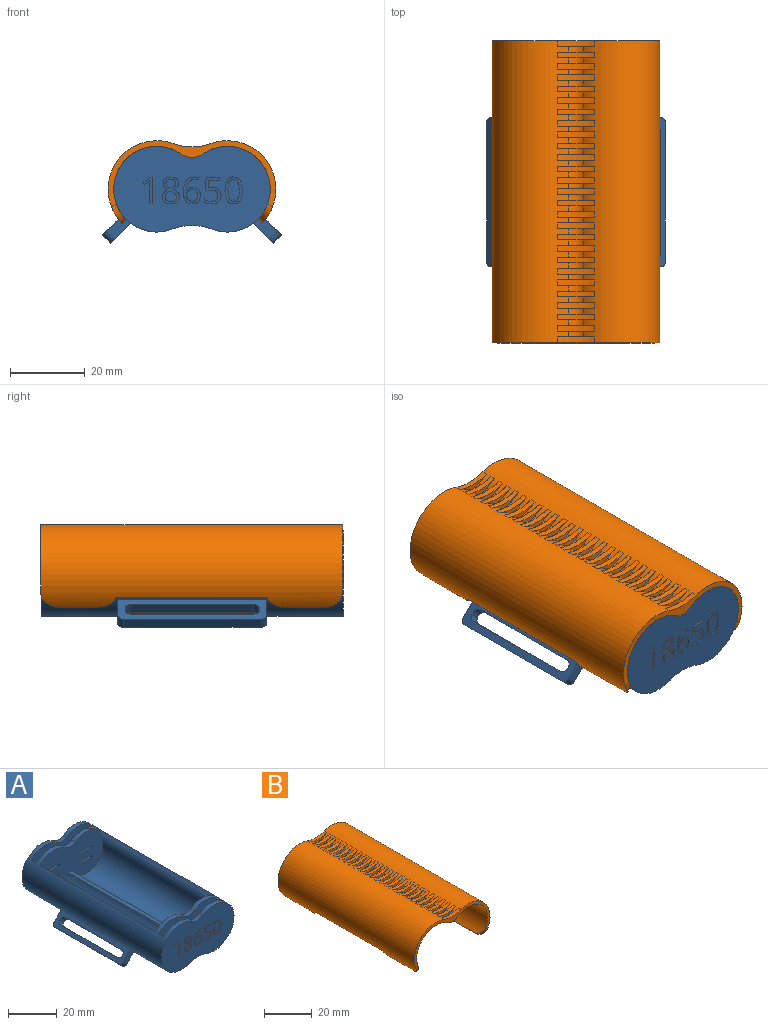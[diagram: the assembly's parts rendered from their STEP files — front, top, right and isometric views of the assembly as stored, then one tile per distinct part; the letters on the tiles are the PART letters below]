
ASSEMBLY  parts=2 mates=1
PART A: 205 faces, bbox 48x81x26 mm
  f0: plane 42x23mm, normal (0,-1,0), area 718.4mm2, adj f3,f9,f52,f88,f89,f90,f91,f92
  f1: plane 40x5.37mm, normal (0.71,0,-0.71), area 175.3mm2, adj f3,f23,f24,f39,f40,f41,f42,f43
  f2: plane 40x5.37mm, normal (-0.71,0,0.71), area 175.3mm2, adj f3,f23,f24,f39,f40,f41,f42,f43
  f3: cylinder r=11.5mm len=81mm, axis (0,1,0), area 2543.9mm2, adj f0,f1,f2,f4,f5,f8,f9,f20
  f4: plane 38x21mm, normal (0,1,0), area 630.6mm2, adj f3,f10,f11,f12,f13,f14,f15,f16
  f5: plane 38x21mm, normal (0,-1,0), area 630.6mm2, adj f3,f6,f7,f8,f10,f11,f12,f13
  f6: plane 67x1.77mm, normal (0,0,1), area 118.3mm2, adj f5,f7,f26,f53
  f7: cylinder r=9.5mm len=67mm, axis (0,1,0), area 2222.9mm2, adj f5,f6,f8,f26
  f8: plane 67x1.41mm, normal (0.71,0,0.71), area 134mm2, adj f3,f5,f7,f26
  f9: cylinder r=15mm len=81mm, axis (0,1,0), area 891mm2, adj f0,f3,f22,f52
  f10: plane 2x1mm, normal (-1,0,0), area 2mm2, adj f4,f5,f11,f13
  f11: plane 6x2mm, normal (0,0,1), area 12mm2, adj f4,f5,f10,f12
  f12: plane 2x1mm, normal (1,0,0), area 2mm2, adj f4,f5,f11,f13
  f13: plane 6x2mm, normal (0,0,-1), area 12mm2, adj f4,f5,f10,f12
  f14: plane 6x2mm, normal (0,0,1), area 12mm2, adj f4,f5,f15,f17
  f15: plane 2x1mm, normal (1,0,0), area 2mm2, adj f4,f5,f14,f16
  f16: plane 6x2mm, normal (0,0,-1), area 12mm2, adj f4,f5,f15,f17
  f17: plane 2x1mm, normal (-1,0,0), area 2mm2, adj f4,f5,f14,f16
  f18: plane 3x1.77mm, normal (0,0,1), area 5.3mm2, adj f4,f19,f21,f63
  f19: cylinder r=9.5mm len=18.12mm, axis (0,-1,0), area 99.5mm2, adj f4,f18,f20,f21
  f20: plane 3x1.41mm, normal (0.71,0,0.71), area 6mm2, adj f3,f4,f19,f21
  f21: plane 38x21mm, normal (0,-1,0), area 641.7mm2, adj f3,f18,f19,f20,f52,f63,f64,f197
  f22: plane 42x23mm, normal (0,1,0), area 797.6mm2, adj f3,f9,f52,f197,f198,f199,f200,f203
  f23: plane 37x2.14mm, normal (-0.71,0,-0.71), area 111.8mm2, adj f1,f2,f48,f49
  f24: plane 6.44x6.44mm, normal (0,1,0), area 18.2mm2, adj f1,f2,f3,f49
  f25: plane 38x21mm, normal (0,-1,0), area 630.6mm2, adj f3,f27,f28,f29,f30,f31,f32,f33
  f26: plane 38x21mm, normal (0,1,0), area 630.6mm2, adj f3,f6,f7,f8,f27,f28,f29,f30
  f27: plane 2x1mm, normal (-1,0,0), area 2mm2, adj f25,f26,f28,f30
  f28: plane 6x2mm, normal (0,0,1), area 12mm2, adj f25,f26,f27,f29
  f29: plane 2x1mm, normal (1,0,0), area 2mm2, adj f25,f26,f28,f30
  f30: plane 6x2mm, normal (0,0,-1), area 12mm2, adj f25,f26,f27,f29
  f31: plane 6x2mm, normal (0,0,1), area 12mm2, adj f25,f26,f32,f34
  f32: plane 2x1mm, normal (1,0,0), area 2mm2, adj f25,f26,f31,f33
  f33: plane 6x2mm, normal (0,0,-1), area 12mm2, adj f25,f26,f32,f34
  f34: plane 2x1mm, normal (-1,0,0), area 2mm2, adj f25,f26,f31,f33
  f35: plane 3x1.77mm, normal (0,0,1), area 5.3mm2, adj f25,f36,f38,f75
  f36: cylinder r=9.5mm len=18.12mm, axis (0,1,0), area 99.5mm2, adj f25,f35,f37,f38
  f37: plane 3x1.41mm, normal (0.71,0,0.71), area 6mm2, adj f3,f25,f36,f38
  f38: plane 38x21mm, normal (0,1,0), area 654.6mm2, adj f3,f35,f36,f37,f52,f75,f76,f202
  f39: plane 6.44x6.44mm, normal (0,-1,0), area 18.2mm2, adj f1,f2,f3,f48
  f40: plane 2.55x2.55mm, normal (0,1,0), area 1.8mm2, adj f1,f2,f44,f47
  f41: plane 33x2.14mm, normal (-0.71,0,-0.71), area 99.7mm2, adj f1,f2,f44,f45
  f42: plane 2.55x2.55mm, normal (0,-1,0), area 1.8mm2, adj f1,f2,f45,f46
  f43: plane 33x2.14mm, normal (0.71,0,0.71), area 99.7mm2, adj f1,f2,f46,f47
  f44: cylinder r=1.5mm len=3.2mm, axis (0.71,0,-0.71), area 7.1mm2, adj f1,f2,f40,f41
  f45: cylinder r=1.5mm len=3.2mm, axis (-0.71,0,0.71), area 7.1mm2, adj f1,f2,f41,f42
  f46: cylinder r=1.5mm len=3.2mm, axis (0.71,0,-0.71), area 7.1mm2, adj f1,f2,f42,f43
  f47: cylinder r=1.5mm len=3.2mm, axis (-0.71,0,0.71), area 7.1mm2, adj f1,f2,f40,f43
  f48: cylinder r=1.5mm len=3.2mm, axis (-0.71,0,0.71), area 7.1mm2, adj f1,f2,f23,f39
  f49: cylinder r=1.5mm len=3.2mm, axis (-0.71,0,0.71), area 7.1mm2, adj f1,f2,f23,f24
  f50: plane 40x5.37mm, normal (-0.71,0,-0.71), area 175.3mm2, adj f52,f65,f66,f77,f78,f79,f80,f81
  f51: plane 40x5.37mm, normal (0.71,0,0.71), area 175.3mm2, adj f52,f65,f66,f77,f78,f79,f80,f81
  f52: cylinder r=11.5mm len=81mm, axis (0,1,0), area 2543.9mm2, adj f0,f4,f5,f9,f21,f22,f25,f26
  f53: cylinder r=9.5mm len=67mm, axis (0,1,0), area 2222.9mm2, adj f5,f6,f26,f54
  f54: plane 67x1.41mm, normal (-0.71,0,0.71), area 134mm2, adj f5,f26,f52,f53
  f55: plane 2x1mm, normal (1,0,0), area 2mm2, adj f4,f5,f56,f58
  f56: plane 6x2mm, normal (0,0,1), area 12mm2, adj f4,f5,f55,f57
  f57: plane 2x1mm, normal (-1,0,0), area 2mm2, adj f4,f5,f56,f58
  f58: plane 6x2mm, normal (0,0,-1), area 12mm2, adj f4,f5,f55,f57
  f59: plane 6x2mm, normal (0,0,1), area 12mm2, adj f4,f5,f60,f62
  f60: plane 2x1mm, normal (-1,0,0), area 2mm2, adj f4,f5,f59,f61
  f61: plane 6x2mm, normal (0,0,-1), area 12mm2, adj f4,f5,f60,f62
  f62: plane 2x1mm, normal (1,0,0), area 2mm2, adj f4,f5,f59,f61
  f63: cylinder r=9.5mm len=18.12mm, axis (0,-1,0), area 99.5mm2, adj f4,f18,f21,f64
  f64: plane 3x1.41mm, normal (-0.71,0,0.71), area 6mm2, adj f4,f21,f52,f63
  f65: plane 37x2.14mm, normal (0.71,0,-0.71), area 111.8mm2, adj f50,f51,f86,f87
  f66: plane 6.44x6.44mm, normal (0,1,0), area 18.2mm2, adj f50,f51,f52,f87
  f67: plane 2x1mm, normal (1,0,0), area 2mm2, adj f25,f26,f68,f70
  f68: plane 6x2mm, normal (0,0,1), area 12mm2, adj f25,f26,f67,f69
  f69: plane 2x1mm, normal (-1,0,0), area 2mm2, adj f25,f26,f68,f70
  f70: plane 6x2mm, normal (0,0,-1), area 12mm2, adj f25,f26,f67,f69
  f71: plane 6x2mm, normal (0,0,1), area 12mm2, adj f25,f26,f72,f74
  f72: plane 2x1mm, normal (-1,0,0), area 2mm2, adj f25,f26,f71,f73
  f73: plane 6x2mm, normal (0,0,-1), area 12mm2, adj f25,f26,f72,f74
  f74: plane 2x1mm, normal (1,0,0), area 2mm2, adj f25,f26,f71,f73
  f75: cylinder r=9.5mm len=18.12mm, axis (0,1,0), area 99.5mm2, adj f25,f35,f38,f76
  f76: plane 3x1.41mm, normal (-0.71,0,0.71), area 6mm2, adj f25,f38,f52,f75
  f77: plane 6.44x6.44mm, normal (0,-1,0), area 18.2mm2, adj f50,f51,f52,f86
  f78: plane 2.55x2.55mm, normal (0,1,0), area 1.8mm2, adj f50,f51,f82,f85
  f79: plane 33x2.14mm, normal (0.71,0,-0.71), area 99.7mm2, adj f50,f51,f82,f83
  f80: plane 2.55x2.55mm, normal (0,-1,0), area 1.8mm2, adj f50,f51,f83,f84
  f81: plane 33x2.14mm, normal (-0.71,0,0.71), area 99.7mm2, adj f50,f51,f84,f85
  f82: cylinder r=1.5mm len=3.2mm, axis (-0.71,0,-0.71), area 7.1mm2, adj f50,f51,f78,f79
  f83: cylinder r=1.5mm len=3.2mm, axis (0.71,0,0.71), area 7.1mm2, adj f50,f51,f79,f80
  f84: cylinder r=1.5mm len=3.2mm, axis (-0.71,0,-0.71), area 7.1mm2, adj f50,f51,f80,f81
  f85: cylinder r=1.5mm len=3.2mm, axis (0.71,0,0.71), area 7.1mm2, adj f50,f51,f78,f81
  f86: cylinder r=1.5mm len=3.2mm, axis (0.71,0,0.71), area 7.1mm2, adj f50,f51,f65,f77
  f87: cylinder r=1.5mm len=3.2mm, axis (0.71,0,0.71), area 7.1mm2, adj f50,f51,f65,f66
  f88: extruded ~1.1x0.5mm, area 0.6mm2, adj f0,f89,f106,f107
  f89: plane 2.11x0.5mm, normal (-1,0,0.08), area 1.1mm2, adj f0,f88,f90,f107
  f90: plane 2.81x0.5mm, normal (0,0,1), area 1.4mm2, adj f0,f89,f91,f107
  f91: plane 0.73x0.5mm, normal (-1,0,0), area 0.4mm2, adj f0,f90,f92,f107
  f92: plane 3.49x0.5mm, normal (0,0,-1), area 1.7mm2, adj f0,f91,f93,f107
  f93: plane 3.28x0.5mm, normal (1,0,-0.08), area 1.6mm2, adj f0,f92,f94,f107
  f94: plane 0.5x0.41mm, normal (0.54,0,0.84), area 0.2mm2, adj f0,f93,f95,f107
  f95: extruded ~1.22x0.5mm, area 0.6mm2, adj f0,f94,f96,f107
  f96: extruded ~1.8x1.47mm, area 1.3mm2, adj f0,f95,f97,f107
  f97: extruded ~1.15x0.5mm, area 0.6mm2, adj f0,f96,f98,f107
  f98: extruded ~1.31x0.5mm, area 0.7mm2, adj f0,f97,f99,f107
  f99: extruded ~0.98x0.5mm, area 0.5mm2, adj f0,f98,f100,f107
  f100: extruded ~0.83x0.5mm, area 0.5mm2, adj f0,f99,f101,f107
  f101: plane 0.77x0.5mm, normal (1,0,0), area 0.4mm2, adj f0,f100,f102,f107
  f102: extruded ~1.81x0.5mm, area 0.9mm2, adj f0,f101,f103,f107
  f103: extruded ~1.91x0.62mm, area 1mm2, adj f0,f102,f104,f107
  f104: extruded ~1.71x0.69mm, area 1mm2, adj f0,f103,f105,f107
  f105: extruded ~1.5x0.64mm, area 0.8mm2, adj f0,f104,f106,f107
  f106: extruded ~1.74x0.55mm, area 0.9mm2, adj f0,f88,f105,f107
  f107: plane 7.11x4.41mm, normal (0,-1,0), area 11.4mm2, adj f88,f89,f90,f91,f92,f93,f94,f95
  f108: extruded ~2.28x0.64mm, area 1.2mm2, adj f0,f109,f132,f133
  f109: extruded ~1.73x0.82mm, area 1mm2, adj f0,f108,f110,f133
  f110: extruded ~1.61x0.63mm, area 0.9mm2, adj f0,f109,f111,f133
  f111: extruded ~1.72x0.6mm, area 0.9mm2, adj f0,f110,f112,f133
  f112: extruded ~1.55x0.54mm, area 0.8mm2, adj f0,f111,f113,f133
  f113: extruded ~1.49x0.57mm, area 0.8mm2, adj f0,f112,f114,f133
  f114: extruded ~1.67x0.83mm, area 1mm2, adj f0,f113,f115,f133
  f115: plane 0.5x0.06mm, normal (0,0,-1), area 0mm2, adj f0,f114,f116,f133
  f116: extruded ~2.21x0.65mm, area 1.2mm2, adj f0,f115,f117,f133
  f117: extruded ~1.72x0.7mm, area 1mm2, adj f0,f116,f118,f133
  f118: extruded ~0.84x0.5mm, area 0.4mm2, adj f0,f117,f119,f133
  f119: plane 0.69x0.5mm, normal (-1,0,0), area 0.3mm2, adj f0,f118,f120,f133
  f120: extruded ~0.85x0.5mm, area 0.4mm2, adj f0,f119,f121,f133
  f121: extruded ~2.38x1.02mm, area 1.3mm2, adj f0,f120,f132,f133
  f122: extruded ~0.8x0.5mm, area 0.4mm2, adj f123,f131,f133,f134
  f123: extruded ~0.68x0.54mm, area 0.4mm2, adj f122,f124,f133,f134
  f124: extruded ~0.92x0.5mm, area 0.5mm2, adj f123,f125,f133,f134
  f125: extruded ~0.65x0.5mm, area 0.3mm2, adj f124,f126,f133,f134
  f126: extruded ~0.57x0.5mm, area 0.4mm2, adj f125,f127,f133,f134
  f127: extruded ~0.79x0.5mm, area 0.4mm2, adj f126,f128,f133,f134
  f128: extruded ~1.05x0.5mm, area 0.6mm2, adj f127,f129,f133,f134
  f129: extruded ~1.09x0.5mm, area 0.6mm2, adj f128,f130,f133,f134
  f130: extruded ~1.24x0.5mm, area 0.7mm2, adj f129,f131,f133,f134
  f131: extruded ~1.06x0.5mm, area 0.6mm2, adj f122,f130,f133,f134
  f132: extruded ~3.09x0.8mm, area 1.6mm2, adj f0,f108,f121,f133
  f133: plane 7.21x4.58mm, normal (0,-1,0), area 12.7mm2, adj f108,f109,f110,f111,f112,f113,f114,f115
  f134: plane 3.16x2.97mm, normal (0,-1,0), area 7.6mm2, adj f122,f123,f124,f125,f126,f127,f128,f129
  f135: extruded ~2.68x0.59mm, area 1.4mm2, adj f0,f136,f150,f151
  f136: extruded ~1.73x0.93mm, area 1mm2, adj f0,f135,f137,f151
  f137: extruded ~1.74x0.89mm, area 1mm2, adj f0,f136,f138,f151
  f138: extruded ~2.72x0.57mm, area 1.4mm2, adj f0,f137,f139,f151
  f139: extruded ~2.69x0.59mm, area 1.4mm2, adj f0,f138,f140,f151
  f140: extruded ~1.72x0.92mm, area 1mm2, adj f0,f139,f141,f151
  f141: extruded ~1.75x0.9mm, area 1mm2, adj f0,f140,f150,f151
  f142: extruded ~2.22x0.5mm, area 1.1mm2, adj f143,f149,f151,f152
  f143: extruded ~1.15x0.69mm, area 0.7mm2, adj f142,f144,f151,f152
  f144: extruded ~1.15x0.7mm, area 0.7mm2, adj f143,f145,f151,f152
  f145: extruded ~2.21x0.5mm, area 1.1mm2, adj f144,f146,f151,f152
  f146: extruded ~2.22x0.5mm, area 1.1mm2, adj f145,f147,f151,f152
  f147: extruded ~1.15x0.71mm, area 0.7mm2, adj f146,f148,f151,f152
  f148: extruded ~1.15x0.7mm, area 0.7mm2, adj f147,f149,f151,f152
  f149: extruded ~2.23x0.5mm, area 1.1mm2, adj f142,f148,f151,f152
  f150: extruded ~2.72x0.57mm, area 1.4mm2, adj f0,f135,f141,f151
  f151: plane 7.22x4.64mm, normal (0,-1,0), area 13mm2, adj f135,f136,f137,f138,f139,f140,f141,f142
  f152: plane 5.84x3.02mm, normal (0,-1,0), area 14.9mm2, adj f142,f143,f144,f145,f146,f147,f148,f149
  f153: extruded ~1.51x0.5mm, area 0.8mm2, adj f0,f154,f183,f184
  f154: extruded ~1.22x0.56mm, area 0.7mm2, adj f0,f153,f155,f184
  f155: extruded ~0.97x0.5mm, area 0.5mm2, adj f0,f154,f156,f184
  f156: extruded ~0.95x0.81mm, area 0.6mm2, adj f0,f155,f157,f184
  f157: extruded ~1.88x1.47mm, area 1.3mm2, adj f0,f156,f158,f184
  f158: extruded ~1.39x0.6mm, area 0.8mm2, adj f0,f157,f159,f184
  f159: extruded ~1.73x0.5mm, area 0.9mm2, adj f0,f158,f160,f184
  f160: extruded ~1.67x0.52mm, area 0.9mm2, adj f0,f159,f161,f184
  f161: extruded ~1.39x0.61mm, area 0.8mm2, adj f0,f160,f162,f184
  f162: extruded ~1.04x0.5mm, area 0.6mm2, adj f0,f161,f163,f184
  f163: extruded ~1.21x0.86mm, area 0.7mm2, adj f0,f162,f164,f184
  f164: extruded ~1.03x0.78mm, area 0.6mm2, adj f0,f163,f165,f184
  f165: extruded ~0.95x0.5mm, area 0.5mm2, adj f0,f164,f166,f184
  f166: extruded ~1.23x0.56mm, area 0.7mm2, adj f0,f165,f183,f184
  f167: extruded ~0.89x0.5mm, area 0.5mm2, adj f168,f181,f184,f186
  f168: extruded ~1.04x0.68mm, area 0.6mm2, adj f167,f169,f184,f186
  f169: extruded ~1.3x0.7mm, area 0.7mm2, adj f168,f170,f184,f186
  f170: extruded ~0.83x0.5mm, area 0.5mm2, adj f169,f171,f184,f186
  f171: extruded ~0.92x0.5mm, area 0.5mm2, adj f170,f172,f184,f186
  f172: extruded ~1.11x0.5mm, area 0.6mm2, adj f171,f173,f184,f186
  f173: extruded ~1.12x0.5mm, area 0.6mm2, adj f172,f181,f184,f186
  f174: extruded ~0.96x0.5mm, area 0.5mm2, adj f175,f182,f184,f185
  f175: extruded ~0.77x0.5mm, area 0.4mm2, adj f174,f176,f184,f185
  f176: extruded ~0.77x0.5mm, area 0.4mm2, adj f175,f177,f184,f185
  f177: extruded ~0.97x0.62mm, area 0.6mm2, adj f176,f178,f184,f185
  f178: extruded ~1.05x0.63mm, area 0.6mm2, adj f177,f179,f184,f185
  f179: extruded ~0.76x0.5mm, area 0.4mm2, adj f178,f180,f184,f185
  f180: extruded ~0.77x0.5mm, area 0.4mm2, adj f179,f182,f184,f185
  f181: extruded ~0.9x0.5mm, area 0.5mm2, adj f167,f173,f184,f186
  f182: extruded ~0.94x0.5mm, area 0.5mm2, adj f174,f180,f184,f185
  f183: extruded ~1.52x0.5mm, area 0.8mm2, adj f0,f153,f166,f184
  f184: plane 7.21x4.61mm, normal (0,-1,0), area 14.6mm2, adj f153,f154,f155,f156,f157,f158,f159,f160
  f185: plane 2.59x2.45mm, normal (0,-1,0), area 4.8mm2, adj f174,f175,f176,f177,f178,f179,f180,f182
  f186: plane 3.04x2.79mm, normal (0,-1,0), area 6.4mm2, adj f167,f168,f169,f170,f171,f172,f173,f181
  f187: plane 7.01x0.5mm, normal (-1,0,0), area 3.5mm2, adj f0,f188,f195,f196
  f188: plane 0.67x0.5mm, normal (0,0,-1), area 0.3mm2, adj f0,f187,f189,f196
  f189: plane 1.86x1.44mm, normal (0.61,0,-0.79), area 1.2mm2, adj f0,f188,f190,f196
  f190: plane 0.55x0.5mm, normal (0.79,0,0.61), area 0.3mm2, adj f0,f189,f191,f196
  f191: extruded ~1.14x0.94mm, area 0.7mm2, adj f0,f190,f192,f196
  f192: extruded ~0.5x0.23mm, area 0.2mm2, adj f0,f191,f193,f196
  f193: extruded ~1.18x0.5mm, area 0.6mm2, adj f0,f192,f194,f196
  f194: plane 5x0.5mm, normal (1,0,0), area 2.5mm2, adj f0,f193,f195,f196
  f195: plane 0.78x0.5mm, normal (0,0,1), area 0.4mm2, adj f0,f187,f194,f196
  f196: plane 7.01x2.53mm, normal (0,-1,0), area 6.7mm2, adj f187,f188,f189,f190,f191,f192,f193,f194
  f197: cylinder r=1.5mm len=3mm, axis (0,1,0), area 10.4mm2, adj f21,f22,f199,f200
  f198: cylinder r=1.5mm len=3mm, axis (0,1,0), area 10.4mm2, adj f21,f22,f199,f200
  f199: cylinder r=5mm len=2mm, axis (0,1,0), area 3.1mm2, adj f21,f22,f197,f198
  f200: cylinder r=5mm len=2mm, axis (0,1,0), area 3.1mm2, adj f21,f22,f197,f198
  f201: cylinder r=5mm len=5.76mm, axis (0,-1,0), area 12.3mm2, adj f3,f25,f26,f52
  f202: cylinder r=5mm len=5.76mm, axis (0,-1,0), area 12.3mm2, adj f0,f3,f38,f52
  f203: cylinder r=5mm len=5.76mm, axis (0,1,0), area 12.3mm2, adj f3,f21,f22,f52
  f204: cylinder r=5mm len=5.76mm, axis (0,1,0), area 12.3mm2, adj f3,f4,f5,f52
PART B: 126 faces, bbox 45x81x23.1 mm
  f0: plane 10.6x1.06mm, normal (-0.71,0,-0.71), area 15.8mm2, adj f1,f34,f118,f121
  f1: cylinder r=13mm len=80.94mm, axis (0,1,0), area 2827.1mm2, adj f0,f2,f3,f4,f5,f6,f7,f8
  f2: cylinder r=3.5mm len=4.03mm, axis (0,1,0), area 6.7mm2, adj f1,f28,f113,f117
  f3: cylinder r=3.5mm len=4.03mm, axis (0,1,0), area 6.7mm2, adj f1,f28,f110,f114
  f4: cylinder r=3.5mm len=4.03mm, axis (0,1,0), area 6.7mm2, adj f1,f28,f107,f111
  f5: cylinder r=3.5mm len=4.03mm, axis (0,1,0), area 6.7mm2, adj f1,f28,f104,f108
  f6: cylinder r=3.5mm len=4.03mm, axis (0,1,0), area 6.7mm2, adj f1,f28,f101,f105
  f7: cylinder r=3.5mm len=4.03mm, axis (0,1,0), area 6.7mm2, adj f1,f28,f98,f102
  f8: cylinder r=3.5mm len=4.03mm, axis (0,1,0), area 6.7mm2, adj f1,f28,f95,f99
  f9: cylinder r=3.5mm len=4.03mm, axis (0,1,0), area 6.7mm2, adj f1,f28,f92,f96
  f10: cylinder r=3.5mm len=4.03mm, axis (0,1,0), area 6.7mm2, adj f1,f28,f89,f93
  f11: cylinder r=3.5mm len=4.03mm, axis (0,1,0), area 6.7mm2, adj f1,f28,f86,f90
  f12: cylinder r=3.5mm len=4.03mm, axis (0,1,0), area 6.7mm2, adj f1,f28,f83,f87
  f13: cylinder r=3.5mm len=4.03mm, axis (0,1,0), area 6.7mm2, adj f1,f28,f80,f84
  f14: cylinder r=3.5mm len=4.03mm, axis (0,1,0), area 6.7mm2, adj f1,f28,f77,f81
  f15: cylinder r=3.5mm len=4.03mm, axis (0,1,0), area 6.7mm2, adj f1,f28,f74,f78
  f16: cylinder r=3.5mm len=4.03mm, axis (0,1,0), area 6.7mm2, adj f1,f28,f71,f75
  f17: cylinder r=3.5mm len=4.03mm, axis (0,1,0), area 6.7mm2, adj f1,f28,f68,f72
  f18: cylinder r=3.5mm len=4.03mm, axis (0,1,0), area 6.7mm2, adj f1,f28,f65,f69
  f19: cylinder r=3.5mm len=4.03mm, axis (0,1,0), area 6.7mm2, adj f1,f28,f62,f66
  f20: cylinder r=3.5mm len=4.03mm, axis (0,1,0), area 6.7mm2, adj f1,f28,f59,f63
  f21: cylinder r=3.5mm len=4.03mm, axis (0,1,0), area 6.7mm2, adj f1,f28,f56,f60
  f22: cylinder r=3.5mm len=4.03mm, axis (0,1,0), area 6.7mm2, adj f1,f28,f53,f57
  f23: cylinder r=3.5mm len=4.03mm, axis (0,1,0), area 6.7mm2, adj f1,f28,f50,f54
  f24: cylinder r=3.5mm len=4.03mm, axis (0,1,0), area 6.7mm2, adj f1,f28,f47,f51
  f25: cylinder r=3.5mm len=4.03mm, axis (0,1,0), area 6.7mm2, adj f1,f28,f44,f48
  f26: cylinder r=3.5mm len=4.03mm, axis (0,1,0), area 6.7mm2, adj f1,f28,f41,f45
  f27: cylinder r=3.5mm len=4.03mm, axis (0,1,0), area 6.7mm2, adj f1,f28,f39,f42
  f28: cylinder r=13mm len=80.94mm, axis (0,1,0), area 2827.1mm2, adj f2,f3,f4,f5,f6,f7,f8,f9
  f29: cylinder r=11.5mm len=80.94mm, axis (0,1,0), area 2602.9mm2, adj f30,f31,f32,f33,f37,f116,f119,f120
  f30: cylinder r=5mm len=80.94mm, axis (0,1,0), area 496.6mm2, adj f29,f32,f34,f116
  f31: plane 10.66x1.06mm, normal (0.71,0,-0.71), area 15.9mm2, adj f28,f29,f124,f125
  f32: plane 45x17.95mm, normal (0,-1,0), area 108mm2, adj f1,f28,f29,f30,f34,f38,f123,f125
  f33: plane 40.42x1.32mm, normal (0.5,0,-0.87), area 60.6mm2, adj f28,f29,f120,f124
  f34: cylinder r=11.5mm len=80.94mm, axis (0,1,0), area 2602.9mm2, adj f0,f30,f32,f35,f36,f116,f118,f121
  f35: plane 10.66x1.06mm, normal (-0.71,0,-0.71), area 15.9mm2, adj f1,f34,f122,f123
  f36: plane 40.42x1.32mm, normal (-0.5,0,-0.87), area 60.6mm2, adj f1,f34,f121,f122
  f37: plane 10.6x1.06mm, normal (0.71,0,-0.71), area 15.8mm2, adj f28,f29,f119,f120
  f38: cylinder r=15mm len=10.18mm, axis (0,-1,0), area 15.6mm2, adj f1,f28,f32,f39
  f39: plane 10.18x2.24mm, normal (0,1,0), area 6.5mm2, adj f1,f27,f28,f38
  f40: cylinder r=15mm len=10.18mm, axis (0,-1,0), area 15.6mm2, adj f1,f28,f41,f42
  f41: plane 10.18x2.24mm, normal (0,1,0), area 6.5mm2, adj f1,f26,f28,f40
  f42: plane 10.18x2.24mm, normal (0,-1,0), area 6.5mm2, adj f1,f27,f28,f40
  f43: cylinder r=15mm len=10.18mm, axis (0,-1,0), area 15.6mm2, adj f1,f28,f44,f45
  f44: plane 10.18x2.24mm, normal (0,1,0), area 6.5mm2, adj f1,f25,f28,f43
  f45: plane 10.18x2.24mm, normal (0,-1,0), area 6.5mm2, adj f1,f26,f28,f43
  f46: cylinder r=15mm len=10.18mm, axis (0,-1,0), area 15.6mm2, adj f1,f28,f47,f48
  f47: plane 10.18x2.24mm, normal (0,1,0), area 6.5mm2, adj f1,f24,f28,f46
  f48: plane 10.18x2.24mm, normal (0,-1,0), area 6.5mm2, adj f1,f25,f28,f46
  f49: cylinder r=15mm len=10.18mm, axis (0,-1,0), area 15.6mm2, adj f1,f28,f50,f51
  f50: plane 10.18x2.24mm, normal (0,1,0), area 6.5mm2, adj f1,f23,f28,f49
  f51: plane 10.18x2.24mm, normal (0,-1,0), area 6.5mm2, adj f1,f24,f28,f49
  f52: cylinder r=15mm len=10.18mm, axis (0,-1,0), area 15.6mm2, adj f1,f28,f53,f54
  f53: plane 10.18x2.24mm, normal (0,1,0), area 6.5mm2, adj f1,f22,f28,f52
  f54: plane 10.18x2.24mm, normal (0,-1,0), area 6.5mm2, adj f1,f23,f28,f52
  f55: cylinder r=15mm len=10.18mm, axis (0,-1,0), area 15.6mm2, adj f1,f28,f56,f57
  f56: plane 10.18x2.24mm, normal (0,1,0), area 6.5mm2, adj f1,f21,f28,f55
  f57: plane 10.18x2.24mm, normal (0,-1,0), area 6.5mm2, adj f1,f22,f28,f55
  f58: cylinder r=15mm len=10.18mm, axis (0,-1,0), area 15.6mm2, adj f1,f28,f59,f60
  f59: plane 10.18x2.24mm, normal (0,1,0), area 6.5mm2, adj f1,f20,f28,f58
  f60: plane 10.18x2.24mm, normal (0,-1,0), area 6.5mm2, adj f1,f21,f28,f58
  f61: cylinder r=15mm len=10.18mm, axis (0,-1,0), area 15.6mm2, adj f1,f28,f62,f63
  f62: plane 10.18x2.24mm, normal (0,1,0), area 6.5mm2, adj f1,f19,f28,f61
  f63: plane 10.18x2.24mm, normal (0,-1,0), area 6.5mm2, adj f1,f20,f28,f61
  f64: cylinder r=15mm len=10.18mm, axis (0,-1,0), area 15.6mm2, adj f1,f28,f65,f66
  f65: plane 10.18x2.24mm, normal (0,1,0), area 6.5mm2, adj f1,f18,f28,f64
  f66: plane 10.18x2.24mm, normal (0,-1,0), area 6.5mm2, adj f1,f19,f28,f64
  f67: cylinder r=15mm len=10.18mm, axis (0,-1,0), area 15.6mm2, adj f1,f28,f68,f69
  f68: plane 10.18x2.24mm, normal (0,1,0), area 6.5mm2, adj f1,f17,f28,f67
  f69: plane 10.18x2.24mm, normal (0,-1,0), area 6.5mm2, adj f1,f18,f28,f67
  f70: cylinder r=15mm len=10.18mm, axis (0,-1,0), area 15.6mm2, adj f1,f28,f71,f72
  f71: plane 10.18x2.24mm, normal (0,1,0), area 6.5mm2, adj f1,f16,f28,f70
  f72: plane 10.18x2.24mm, normal (0,-1,0), area 6.5mm2, adj f1,f17,f28,f70
  f73: cylinder r=15mm len=10.18mm, axis (0,-1,0), area 15.6mm2, adj f1,f28,f74,f75
  f74: plane 10.18x2.24mm, normal (0,1,0), area 6.5mm2, adj f1,f15,f28,f73
  f75: plane 10.18x2.24mm, normal (0,-1,0), area 6.5mm2, adj f1,f16,f28,f73
  f76: cylinder r=15mm len=10.18mm, axis (0,-1,0), area 15.6mm2, adj f1,f28,f77,f78
  f77: plane 10.18x2.24mm, normal (0,1,0), area 6.5mm2, adj f1,f14,f28,f76
  f78: plane 10.18x2.24mm, normal (0,-1,0), area 6.5mm2, adj f1,f15,f28,f76
  f79: cylinder r=15mm len=10.18mm, axis (0,-1,0), area 15.6mm2, adj f1,f28,f80,f81
  f80: plane 10.18x2.24mm, normal (0,1,0), area 6.5mm2, adj f1,f13,f28,f79
  f81: plane 10.18x2.24mm, normal (0,-1,0), area 6.5mm2, adj f1,f14,f28,f79
  f82: cylinder r=15mm len=10.18mm, axis (0,-1,0), area 15.6mm2, adj f1,f28,f83,f84
  f83: plane 10.18x2.24mm, normal (0,1,0), area 6.5mm2, adj f1,f12,f28,f82
  f84: plane 10.18x2.24mm, normal (0,-1,0), area 6.5mm2, adj f1,f13,f28,f82
  f85: cylinder r=15mm len=10.18mm, axis (0,-1,0), area 15.6mm2, adj f1,f28,f86,f87
  f86: plane 10.18x2.24mm, normal (0,1,0), area 6.5mm2, adj f1,f11,f28,f85
  f87: plane 10.18x2.24mm, normal (0,-1,0), area 6.5mm2, adj f1,f12,f28,f85
  f88: cylinder r=15mm len=10.18mm, axis (0,-1,0), area 15.6mm2, adj f1,f28,f89,f90
  f89: plane 10.18x2.24mm, normal (0,1,0), area 6.5mm2, adj f1,f10,f28,f88
  f90: plane 10.18x2.24mm, normal (0,-1,0), area 6.5mm2, adj f1,f11,f28,f88
  f91: cylinder r=15mm len=10.18mm, axis (0,-1,0), area 15.6mm2, adj f1,f28,f92,f93
  f92: plane 10.18x2.24mm, normal (0,1,0), area 6.5mm2, adj f1,f9,f28,f91
  f93: plane 10.18x2.24mm, normal (0,-1,0), area 6.5mm2, adj f1,f10,f28,f91
  f94: cylinder r=15mm len=10.18mm, axis (0,-1,0), area 15.6mm2, adj f1,f28,f95,f96
  f95: plane 10.18x2.24mm, normal (0,1,0), area 6.5mm2, adj f1,f8,f28,f94
  f96: plane 10.18x2.24mm, normal (0,-1,0), area 6.5mm2, adj f1,f9,f28,f94
  f97: cylinder r=15mm len=10.18mm, axis (0,-1,0), area 15.6mm2, adj f1,f28,f98,f99
  f98: plane 10.18x2.24mm, normal (0,1,0), area 6.5mm2, adj f1,f7,f28,f97
  f99: plane 10.18x2.24mm, normal (0,-1,0), area 6.5mm2, adj f1,f8,f28,f97
  f100: cylinder r=15mm len=10.18mm, axis (0,-1,0), area 15.6mm2, adj f1,f28,f101,f102
  f101: plane 10.18x2.24mm, normal (0,1,0), area 6.5mm2, adj f1,f6,f28,f100
  f102: plane 10.18x2.24mm, normal (0,-1,0), area 6.5mm2, adj f1,f7,f28,f100
  f103: cylinder r=15mm len=10.18mm, axis (0,-1,0), area 15.6mm2, adj f1,f28,f104,f105
  f104: plane 10.18x2.24mm, normal (0,1,0), area 6.5mm2, adj f1,f5,f28,f103
  f105: plane 10.18x2.24mm, normal (0,-1,0), area 6.5mm2, adj f1,f6,f28,f103
  f106: cylinder r=15mm len=10.18mm, axis (0,-1,0), area 15.6mm2, adj f1,f28,f107,f108
  f107: plane 10.18x2.24mm, normal (0,1,0), area 6.5mm2, adj f1,f4,f28,f106
  f108: plane 10.18x2.24mm, normal (0,-1,0), area 6.5mm2, adj f1,f5,f28,f106
  f109: cylinder r=15mm len=10.18mm, axis (0,-1,0), area 15.6mm2, adj f1,f28,f110,f111
  f110: plane 10.18x2.24mm, normal (0,1,0), area 6.5mm2, adj f1,f3,f28,f109
  f111: plane 10.18x2.24mm, normal (0,-1,0), area 6.5mm2, adj f1,f4,f28,f109
  f112: cylinder r=15mm len=10.18mm, axis (0,-1,0), area 15.6mm2, adj f1,f28,f113,f114
  f113: plane 10.18x2.24mm, normal (0,1,0), area 6.5mm2, adj f1,f2,f28,f112
  f114: plane 10.18x2.24mm, normal (0,-1,0), area 6.5mm2, adj f1,f3,f28,f112
  f115: cylinder r=15mm len=10.18mm, axis (0,-1,0), area 15.6mm2, adj f1,f28,f116,f117
  f116: plane 45x17.95mm, normal (0,1,0), area 108mm2, adj f1,f28,f29,f30,f34,f115,f118,f119
  f117: plane 10.18x2.24mm, normal (0,-1,0), area 6.5mm2, adj f1,f2,f28,f115
  f118: cylinder r=5mm len=5.41mm, axis (-0.71,0,0.71), area 12.3mm2, adj f0,f1,f34,f116
  f119: cylinder r=5mm len=5.41mm, axis (0.71,0,0.71), area 12.3mm2, adj f28,f29,f37,f116
  f120: bspline ~4.78x4.52mm, area 9mm2, adj f28,f29,f33,f37
  f121: bspline ~6.31x4.98mm, area 8.9mm2, adj f0,f1,f34,f36
  f122: bspline ~4.78x4.52mm, area 9mm2, adj f1,f34,f35,f36
  f123: cylinder r=5mm len=5.41mm, axis (0.71,0,-0.71), area 12.3mm2, adj f1,f32,f34,f35
  f124: bspline ~6.31x4.98mm, area 8.9mm2, adj f28,f29,f31,f33
  f125: cylinder r=5mm len=5.41mm, axis (-0.71,0,-0.71), area 12.3mm2, adj f28,f29,f31,f32
PLACE A t=(0,-7,24.74)mm
PLACE B t=(0,-40.33,24.74)mm
MATE slider B.f2 <-> A.f201  axis (0,-1,0) through (0,-80.83,38.23)mm
